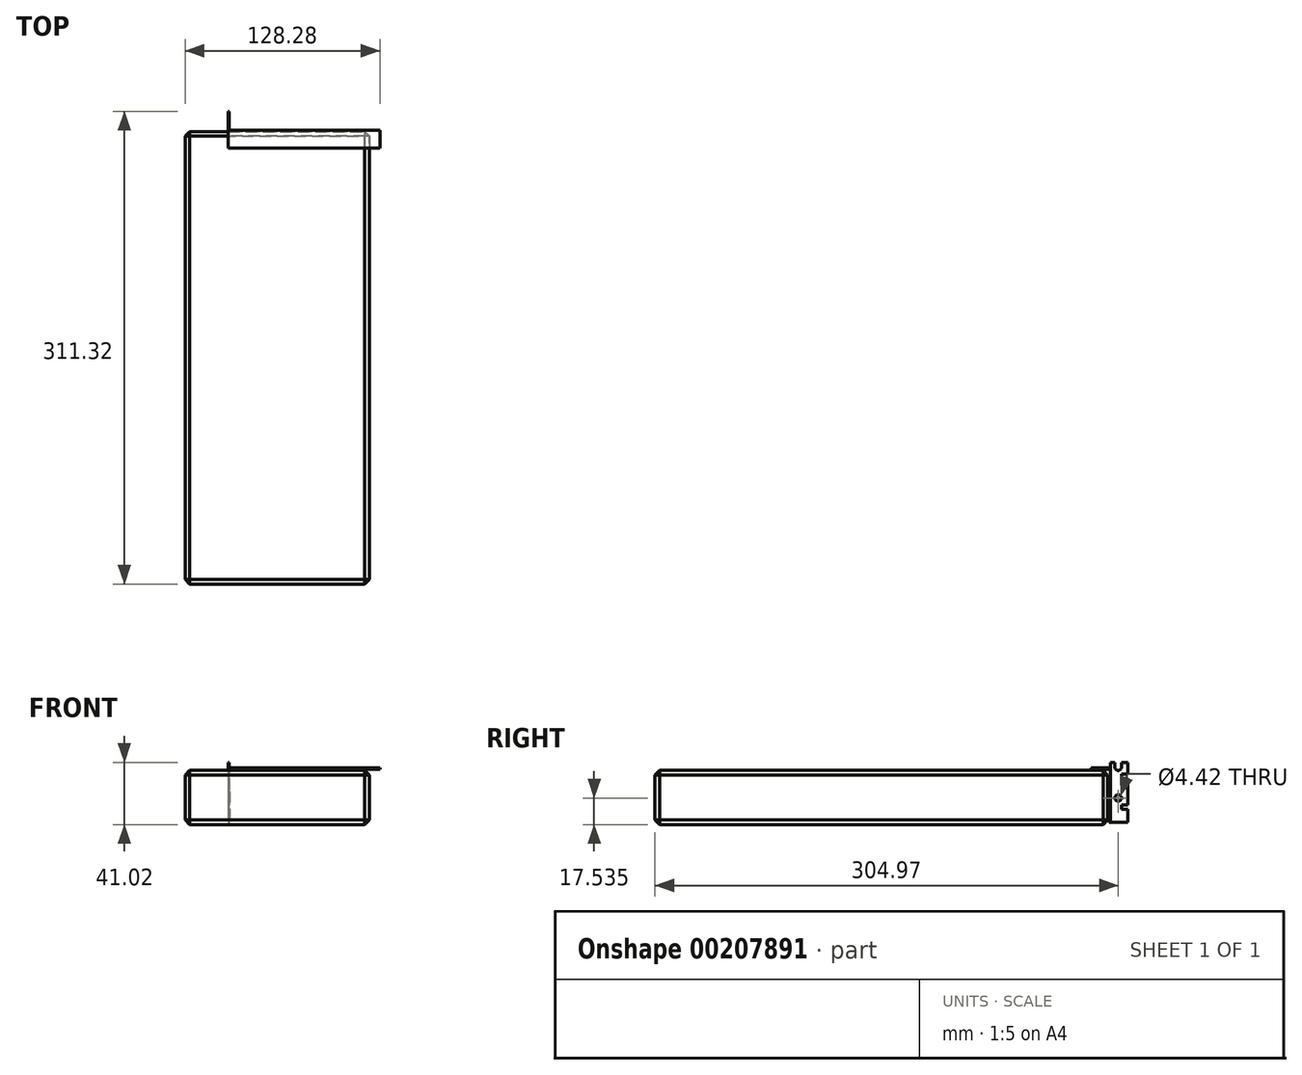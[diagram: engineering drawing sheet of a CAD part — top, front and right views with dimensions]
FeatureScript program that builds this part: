
annotation { "Feature Type Name" : "Feature", "Feature Type Description" : "" }
export const myFeature = defineFeature(function(context is Context, id is Id, definition is map)
    precondition{}
    {
        {
            var Q0;
            Q0=qCreatedBy(makeId("Top.planeOp"),FACE);
            var sketch = newSketch(context, id + "F0", { "sketchPlane" : qUnion([Q0])});
            skLineSegment(sketch, "E0.bottom", {"start": v(-137.4, -240.84) * mm, "end": v(-114.55, -240.84) * mm});
            skLineSegment(sketch, "E0.top", {"start": v(-137.4, 57.16) * mm, "end": v(-114.55, 57.16) * mm});
            skLineSegment(sketch, "E0.left", {"start": v(-137.4, -240.84) * mm, "end": v(-137.4, 57.16) * mm});
            skLineSegment(sketch, "E0.right", {"start": v(-114.55, -240.84) * mm, "end": v(-114.55, 57.16) * mm});
            skPoint(sketch, "E1", {"position": v(-3.4, -240.84) * mm});
            skLineSegment(sketch, "E2", {"start": v(11.76, 58.2) * mm, "end": v(11.76, 59.05) * mm});
            skLineSegment(sketch, "E3", {"start": v(11.76, 59.05) * mm, "end": v(-108.26, 59.05) * mm});
            skLineSegment(sketch, "E4", {"start": v(-108.26, 59.05) * mm, "end": v(-108.26, 70.48) * mm});
            skLineSegment(sketch, "E5", {"start": v(-108.26, 70.48) * mm, "end": v(-109.12, 70.48) * mm});
            skLineSegment(sketch, "E6.bottom", {"start": v(-114.55, -240.84) * mm, "end": v(-16.15, -240.84) * mm});
            skLineSegment(sketch, "E6.top", {"start": v(-114.55, 57.16) * mm, "end": v(-16.15, 57.16) * mm});
            skLineSegment(sketch, "E6.right", {"start": v(-16.15, -240.84) * mm, "end": v(-16.15, 57.16) * mm});
            skLineSegment(sketch, "E7.bottom", {"start": v(-16.15, 57.16) * mm, "end": v(-7.9, 57.16) * mm});
            skLineSegment(sketch, "E7.top", {"start": v(-16.15, 42.16) * mm, "end": v(-7.9, 42.16) * mm});
            skLineSegment(sketch, "E7.left", {"start": v(-16.15, 57.16) * mm, "end": v(-16.15, 42.16) * mm});
            skLineSegment(sketch, "E7.right", {"start": v(-7.9, 57.16) * mm, "end": v(-7.9, 42.16) * mm});
            skPoint(sketch, "E8", {"position": v(-7.9, -240.84) * mm});
            skLineSegment(sketch, "E9.bottom", {"start": v(-16.15, 23.8) * mm, "end": v(-7.9, 23.8) * mm});
            skLineSegment(sketch, "E9.top", {"start": v(-16.15, 15.8) * mm, "end": v(-7.9, 15.8) * mm});
            skLineSegment(sketch, "E9.left", {"start": v(-16.15, 23.8) * mm, "end": v(-16.15, 15.8) * mm});
            skLineSegment(sketch, "E9.right", {"start": v(-7.9, 23.8) * mm, "end": v(-7.9, 15.8) * mm});
            skPoint(sketch, "E10", {"position": v(-3.4, 57.16) * mm});
            skLineSegment(sketch, "E11", {"start": v(-16.15, 12.15) * mm, "end": v(-3.4, 12.15) * mm});
            skLineSegment(sketch, "E12", {"start": v(-3.4, 12.15) * mm, "end": v(-3.4, 0.95) * mm});
            skLineSegment(sketch, "E13", {"start": v(-3.4, 0.95) * mm, "end": v(-11.8, 0.95) * mm});
            skLineSegment(sketch, "E14", {"start": v(-11.8, 0.95) * mm, "end": v(-11.8, -0.95) * mm});
            skLineSegment(sketch, "E15", {"start": v(-11.8, -0.95) * mm, "end": v(-3.4, -0.95) * mm});
            skLineSegment(sketch, "E16", {"start": v(-3.4, -0.95) * mm, "end": v(-3.4, -72.15) * mm});
            skLineSegment(sketch, "E17", {"start": v(-3.4, -72.15) * mm, "end": v(-16.15, -72.15) * mm});
            skPoint(sketch, "E18", {"position": v(-11.8, 0) * mm});
            skArc(sketch, "E19", {"start": v(-14.32, 15.8) * mm, "mid": v(-16.15, 13.98) * mm, "end": v(-14.32, 12.15) * mm});
            skArc(sketch, "E20", {"start": v(-10.85, 0.95) * mm, "mid": v(-11.8, 0) * mm, "end": v(-10.85, -0.95) * mm});
            skLineSegment(sketch, "E21", {"start": v(-16.15, -81.9) * mm, "end": v(-11.35, -81.9) * mm});
            skLineSegment(sketch, "E22", {"start": v(-11.35, -81.9) * mm, "end": v(-11.35, -87.6) * mm});
            skLineSegment(sketch, "E23", {"start": v(-11.35, -87.6) * mm, "end": v(-8.77, -87.6) * mm});
            skLineSegment(sketch, "E24", {"start": v(-8.77, -87.6) * mm, "end": v(-6.35, -86.2) * mm});
            skLineSegment(sketch, "E25", {"start": v(-6.35, -86.2) * mm, "end": v(-6.35, -74.9) * mm});
            skLineSegment(sketch, "E26", {"start": v(-6.35, -74.9) * mm, "end": v(-12.38, -74.9) * mm});
            skLineSegment(sketch, "E27", {"start": v(-12.38, -74.9) * mm, "end": v(-12.38, -72.15) * mm});
            skArc(sketch, "E28", {"start": v(-11, -72.15) * mm, "mid": v(-12.38, -73.53) * mm, "end": v(-11, -74.9) * mm});
            skLineSegment(sketch, "E29", {"start": v(-108.26, 59.05) * mm, "end": v(-109.12, 59.05) * mm});
            skLineSegment(sketch, "E30", {"start": v(-109.12, 70.48) * mm, "end": v(-109.12, 59.05) * mm});
            skLineSegment(sketch, "E31", {"start": v(-109.12, 58.2) * mm, "end": v(-109.12, 59.05) * mm});
            skLineSegment(sketch, "E32", {"start": v(-108.26, 59.05) * mm, "end": v(-108.26, 58.2) * mm});
            skLineSegment(sketch, "E33", {"start": v(-108.26, 58.2) * mm, "end": v(-109.12, 58.2) * mm});
            skLineSegment(sketch, "E34", {"start": v(-108.26, 58.2) * mm, "end": v(11.76, 58.2) * mm});
            skPoint(sketch, "E35", {"position": v(0, 0) * mm});
            skPoint(sketch, "E36", {"position": v(0, 57.16) * mm});
            skSolve(sketch);
        }
        {
            var Q0;
            {var subQ7=sQuery(id+"F0.wireOp",EDGE,"E6.bottom");Q0=makeQuery(id+"F0.imprint","IMPRINT",FACE,{"disambiguationData":[TD([[makeQuery(id+"F0.imprint","IMPRINT",EDGE,{"derivedFrom":subQ7}),1.0]])]});}
            var Q1;
            Q1=makeQuery(id+"F0.imprint","IMPRINT",FACE,{"disambiguationData":[TD([[makeQuery(id+"F0.imprint","IMPRINT",EDGE,{"derivedFrom":sQuery(id+"F0.wireOp",EDGE,"E0.bottom")}),1.0]])]});
            var Q2;
            {var subQ5=sQuery(id+"F0.wireOp",EDGE,"E21");Q2=makeQuery(id+"F0.imprint","IMPRINT",FACE,{"disambiguationData":[TD([[makeQuery(id+"F0.imprint","IMPRINT",EDGE,{"derivedFrom":subQ5}),1.0]])]});}
            var Q3;
            {var subQ0=sQuery(id+"F0.wireOp",EDGE,"E27");var subQ1=sQuery(id+"F0.wireOp",EDGE,"E26");var subQ2=makeQuery(id+"F0.imprint","INTERSECT",VERTEX,{"derivedFrom":[subQ1,subQ0]});Q3=makeQuery(id+"F0.imprint","IMPRINT",FACE,{"disambiguationData":[TD([[makeQuery(id+"F0.imprint","IMPRINT",EDGE,{"disambiguationData":[TD([[subQ2,1.0]])],"derivedFrom":subQ1}),-1.0]])]});}
            var Q4;
            {var subQ0=sQuery(id+"F0.wireOp",EDGE,"E27");var subQ1=sQuery(id+"F0.wireOp",EDGE,"E17");var subQ2=makeQuery(id+"F0.imprint","INTERSECT",VERTEX,{"derivedFrom":[subQ1,subQ0]});Q4=makeQuery(id+"F0.imprint","IMPRINT",FACE,{"disambiguationData":[TD([[makeQuery(id+"F0.imprint","IMPRINT",EDGE,{"disambiguationData":[TD([[subQ2,1.0]])],"derivedFrom":subQ1}),1.0]])]});}
            var Q5;
            {var subQ0=sQuery(id+"F0.wireOp",EDGE,"E15");var subQ1=sQuery(id+"F0.wireOp",EDGE,"E14");var subQ2=makeQuery(id+"F0.imprint","INTERSECT",VERTEX,{"derivedFrom":[subQ1,subQ0]});Q5=makeQuery(id+"F0.imprint","IMPRINT",FACE,{"disambiguationData":[TD([[makeQuery(id+"F0.imprint","IMPRINT",EDGE,{"disambiguationData":[TD([[subQ2,1.0]])],"derivedFrom":subQ1}),1.0]])]});}
            var Q6;
            {var subQ0=sQuery(id+"F0.wireOp",EDGE,"E14");var subQ1=sQuery(id+"F0.wireOp",EDGE,"E13");var subQ2=makeQuery(id+"F0.imprint","INTERSECT",VERTEX,{"derivedFrom":[subQ1,subQ0]});Q6=makeQuery(id+"F0.imprint","IMPRINT",FACE,{"disambiguationData":[TD([[makeQuery(id+"F0.imprint","IMPRINT",EDGE,{"disambiguationData":[TD([[subQ2,1.0]])],"derivedFrom":subQ1}),1.0]])]});}
            var Q7;
            {var subQ7=sQuery(id+"F0.wireOp",EDGE,"E12");Q7=makeQuery(id+"F0.imprint","IMPRINT",FACE,{"disambiguationData":[TD([[makeQuery(id+"F0.imprint","IMPRINT",EDGE,{"derivedFrom":subQ7}),-1.0]])]});}
            var Q8;
            {var subQ0=sQuery(id+"F0.wireOp",EDGE,"E11");var subQ1=sQuery(id+"F0.wireOp",EDGE,"E6.right");var subQ2=makeQuery(id+"F0.imprint","INTERSECT",VERTEX,{"derivedFrom":[subQ1,subQ0]});Q8=makeQuery(id+"F0.imprint","IMPRINT",FACE,{"disambiguationData":[TD([[makeQuery(id+"F0.imprint","IMPRINT",EDGE,{"disambiguationData":[TD([[subQ2,-1.0]])],"derivedFrom":subQ1}),-1.0]])]});}
            var Q9;
            {var subQ0=sQuery(id+"F0.wireOp",EDGE,"E9.top");var subQ3=sQuery(id+"F0.wireOp",EDGE,"E19");var subQ5=makeQuery(id+"F0.imprint","INTERSECT",VERTEX,{"derivedFrom":[subQ0,subQ3]});Q9=makeQuery(id+"F0.imprint","IMPRINT",FACE,{"disambiguationData":[TD([[makeQuery(id+"F0.imprint","IMPRINT",EDGE,{"disambiguationData":[TD([[subQ5,-1.0]])],"derivedFrom":subQ3}),-1.0]])]});}
            var Q10;
            Q10=makeQuery(id+"F0.imprint","IMPRINT",FACE,{"disambiguationData":[TD([[makeQuery(id+"F0.imprint","IMPRINT",EDGE,{"derivedFrom":sQuery(id+"F0.wireOp",EDGE,"E9.bottom")}),-1.0]])]});
            var Q11;
            Q11=makeQuery(id+"F0.imprint","IMPRINT",FACE,{"disambiguationData":[TD([[makeQuery(id+"F0.imprint","IMPRINT",EDGE,{"derivedFrom":sQuery(id+"F0.wireOp",EDGE,"E7.bottom")}),-1.0]])]});
            extrude(context, id + "F1", {"entities" : qUnion([Q0, Q1, Q2, Q3, Q4, Q5, Q6, Q7, Q8, Q9, Q10, Q11]), "endBound" : BoundingType.SYMMETRIC, "depth" : 1.57 * mm});
        }
        {
            var Q0;
            Q0=makeQuery(id+"F0.imprint","IMPRINT",FACE,{"disambiguationData":[TD([[makeQuery(id+"F0.imprint","IMPRINT",EDGE,{"derivedFrom":sQuery(id+"F0.wireOp",EDGE,"E2")}),1.0]])]});
            extrude(context, id + "F2", {"entities" : qUnion([Q0]), "depth" : 10 * mm, "hasSecondDirection" : true, "secondDirectionOppositeDirection" : true, "secondDirectionDepth" : 40 * mm});
        }
        {
            var Q0;
            Q0=makeQuery(id+"F2.opExtrude","SWEPT_FACE",FACE,{"disambiguationData":[OSD([sQuery(id+"F0.wireOp",EDGE,"E3")])]});
            var sketch = newSketch(context, id + "F3", { "sketchPlane" : qUnion([Q0])});
            skLineSegment(sketch, "E37", {"start": v(-4.49, -2.06) * mm, "end": v(-11.76, -2.06) * mm});
            skLineSegment(sketch, "E38", {"start": v(-11.76, -2.06) * mm, "end": v(-11.76, -12.25) * mm});
            skLineSegment(sketch, "E39", {"start": v(-11.76, -12.25) * mm, "end": v(-4.49, -12.25) * mm});
            skLineSegment(sketch, "E40", {"start": v(-4.49, -12.25) * mm, "end": v(-0.38, -16.37) * mm});
            skLineSegment(sketch, "E41", {"start": v(-0.38, -16.36) * mm, "end": v(101.78, -16.36) * mm});
            skLineSegment(sketch, "E42", {"start": v(108.26, -13.82) * mm, "end": v(108.26, 5.23) * mm});
            skLineSegment(sketch, "E43", {"start": v(108.26, 5.23) * mm, "end": v(105.34, 5.23) * mm});
            skLineSegment(sketch, "E44", {"start": v(103.7, 2.06) * mm, "end": v(-0.37, 2.05) * mm});
            skLineSegment(sketch, "E45", {"start": v(-0.37, 2.05) * mm, "end": v(-4.49, -2.06) * mm});
            skLineSegment(sketch, "E46.bottom", {"start": v(7.9, 0.79) * mm, "end": v(114.55, 0.79) * mm});
            skLineSegment(sketch, "E46.top", {"start": v(7.9, -0.78) * mm, "end": v(114.55, -0.78) * mm});
            skLineSegment(sketch, "E46.left", {"start": v(7.9, 0.78) * mm, "end": v(7.9, -0.78) * mm});
            skLineSegment(sketch, "E46.right", {"start": v(114.55, 0.79) * mm, "end": v(114.55, -0.78) * mm});
            skPoint(sketch, "E47", {"position": v(7.9, 0) * mm});
            skLineSegment(sketch, "E48", {"start": v(108.26, -13.82) * mm, "end": v(104.32, -13.82) * mm});
            skLineSegment(sketch, "E49", {"start": v(104.32, -13.82) * mm, "end": v(101.78, -16.36) * mm});
            skLineSegment(sketch, "E50", {"start": v(103.7, 2.05) * mm, "end": v(103.7, 3.59) * mm});
            skLineSegment(sketch, "E51", {"start": v(103.7, 3.59) * mm, "end": v(105.34, 5.23) * mm});
            skPoint(sketch, "E52", {"position": v(0, 0) * mm});
            skLineSegment(sketch, "E53", {"start": v(-11.76, -22.39) * mm, "end": v(-11.76, -32.58) * mm});
            skLineSegment(sketch, "E54", {"start": v(-11.76, -32.57) * mm, "end": v(-4.49, -32.57) * mm});
            skLineSegment(sketch, "E55", {"start": v(-4.49, -32.57) * mm, "end": v(-0.38, -36.69) * mm});
            skLineSegment(sketch, "E56", {"start": v(-0.38, -36.69) * mm, "end": v(101.78, -36.68) * mm});
            skLineSegment(sketch, "E57", {"start": v(104.32, -34.14) * mm, "end": v(101.78, -36.68) * mm});
            skLineSegment(sketch, "E58", {"start": v(104.32, -34.14) * mm, "end": v(108.26, -34.14) * mm});
            skLineSegment(sketch, "E59", {"start": v(108.26, -34.14) * mm, "end": v(108.26, -15.1) * mm});
            skLineSegment(sketch, "E60", {"start": v(108.26, -15.1) * mm, "end": v(105.34, -15.1) * mm});
            skLineSegment(sketch, "E61", {"start": v(105.34, -15.1) * mm, "end": v(103.7, -16.73) * mm});
            skLineSegment(sketch, "E62", {"start": v(103.7, -16.73) * mm, "end": v(103.7, -18.26) * mm});
            skLineSegment(sketch, "E63", {"start": v(103.7, -18.26) * mm, "end": v(-0.37, -18.27) * mm});
            skLineSegment(sketch, "E64", {"start": v(-11.76, -22.39) * mm, "end": v(-4.49, -22.39) * mm});
            skLineSegment(sketch, "E65", {"start": v(-4.49, -22.39) * mm, "end": v(-0.37, -18.27) * mm});
            skLineSegment(sketch, "E66", {"start": v(-0.38, -16.37) * mm, "end": v(-0.37, -18.27) * mm});
            skLineSegment(sketch, "E67", {"start": v(108.26, -13.82) * mm, "end": v(108.26, -15.1) * mm});
            skSolve(sketch);
        }
        {
            var Q0;
            Q0 = qSketchRegion(id + "F3", true);
            extrude(context, id + "F4", {"entities" : qUnion([Q0]), "operationType" : NewBodyOperationType.INTERSECT, "oppositeDirection" : true, "depth" : 5 * mm});
        }
        {
            var Q0;
            Q0=makeQuery(id+"F0.imprint","IMPRINT",FACE,{"disambiguationData":[TD([[makeQuery(id+"F0.imprint","IMPRINT",EDGE,{"derivedFrom":sQuery(id+"F0.wireOp",EDGE,"E29")}),1.0]])]});
            var Q1;
            Q1=makeQuery(id+"F0.imprint","IMPRINT",FACE,{"disambiguationData":[TD([[makeQuery(id+"F0.imprint","IMPRINT",EDGE,{"derivedFrom":sQuery(id+"F0.wireOp",EDGE,"E4")}),1.0]])]});
            extrude(context, id + "F5", {"entities" : qUnion([Q0, Q1]), "depth" : 10 * mm, "hasSecondDirection" : true, "secondDirectionOppositeDirection" : true, "secondDirectionDepth" : 40 * mm});
        }
        {
            var Q0;
            Q0=makeQuery(id+"F5.opExtrude","SWEPT_FACE",FACE,{"disambiguationData":[OSD([sQuery(id+"F0.wireOp",EDGE,"E30"),sQuery(id+"F0.wireOp",EDGE,"E31")])]});
            var sketch = newSketch(context, id + "F6", { "sketchPlane" : qUnion([Q0])});
            skLineSegment(sketch, "E68", {"start": v(-70.48, 5.23) * mm, "end": v(-70.48, -2.4) * mm});
            skLineSegment(sketch, "E69", {"start": v(-70.48, -2.4) * mm, "end": v(-66.29, -2.4) * mm});
            skLineSegment(sketch, "E70", {"start": v(-66.3, -2.4) * mm, "end": v(-66.3, -5.44) * mm});
            skLineSegment(sketch, "E71", {"start": v(-66.3, -5.44) * mm, "end": v(-70.48, -5.44) * mm});
            skLineSegment(sketch, "E72", {"start": v(-70.48, -5.44) * mm, "end": v(-70.48, -13.83) * mm});
            skLineSegment(sketch, "E73", {"start": v(-58.19, -13.83) * mm, "end": v(-58.19, 5.22) * mm});
            skLineSegment(sketch, "E74", {"start": v(-61.92, 5.22) * mm, "end": v(-61.92, -0.16) * mm});
            skLineSegment(sketch, "E75", {"start": v(-61.92, -0.15) * mm, "end": v(-66.34, -0.16) * mm});
            skLineSegment(sketch, "E76", {"start": v(-66.34, -0.16) * mm, "end": v(-66.34, 5.23) * mm});
            skLineSegment(sketch, "E77", {"start": v(-66.34, 5.23) * mm, "end": v(-70.48, 5.23) * mm});
            skPoint(sketch, "E78", {"position": v(-70.48, -16.37) * mm});
            skArc(sketch, "E79", {"start": v(-66.34, 2.06) * mm, "mid": v(-64.13, -0.16) * mm, "end": v(-61.92, 2.06) * mm});
            skLineSegment(sketch, "E80.bottom", {"start": v(-57.16, 0.79) * mm, "end": v(0, 0.79) * mm});
            skLineSegment(sketch, "E80.top", {"start": v(-57.16, -0.79) * mm, "end": v(0, -0.79) * mm});
            skLineSegment(sketch, "E80.left", {"start": v(-57.16, 0.79) * mm, "end": v(-57.16, -0.79) * mm});
            skPoint(sketch, "E81", {"position": v(-57.16, 0) * mm});
            skLineSegment(sketch, "E82.bottom", {"start": v(-46.48, 1.65) * mm, "end": v(-58.19, 1.65) * mm});
            skLineSegment(sketch, "E82.top", {"start": v(-46.48, 0.78) * mm, "end": v(-58.19, 0.78) * mm});
            skLineSegment(sketch, "E82.left", {"start": v(-46.48, 1.65) * mm, "end": v(-46.48, 0.78) * mm});
            skLineSegment(sketch, "E82.right", {"start": v(-58.19, 1.65) * mm, "end": v(-58.19, 0.78) * mm});
            skLineSegment(sketch, "E83", {"start": v(-59.05, 5.22) * mm, "end": v(-59.05, -13.83) * mm});
            skLineSegment(sketch, "E84", {"start": v(-61.92, 5.22) * mm, "end": v(-59.05, 5.22) * mm});
            skLineSegment(sketch, "E85", {"start": v(-59.05, 5.22) * mm, "end": v(-58.19, 5.22) * mm});
            skPoint(sketch, "E86", {"position": v(0, 0) * mm});
            skLineSegment(sketch, "E87", {"start": v(-59.05, -15.1) * mm, "end": v(-70.48, -15.1) * mm});
            skLineSegment(sketch, "E88", {"start": v(-70.48, -15.1) * mm, "end": v(-70.48, -22.71) * mm});
            skLineSegment(sketch, "E89", {"start": v(-70.48, -22.71) * mm, "end": v(-66.3, -22.71) * mm});
            skLineSegment(sketch, "E90", {"start": v(-66.3, -22.71) * mm, "end": v(-66.3, -25.76) * mm});
            skLineSegment(sketch, "E91", {"start": v(-66.3, -25.76) * mm, "end": v(-70.48, -25.76) * mm});
            skLineSegment(sketch, "E92", {"start": v(-70.48, -25.76) * mm, "end": v(-70.48, -34.14) * mm});
            skLineSegment(sketch, "E93", {"start": v(-70.48, -34.14) * mm, "end": v(-59.05, -34.14) * mm});
            skLineSegment(sketch, "E94", {"start": v(-59.05, -34.14) * mm, "end": v(-59.05, -15.1) * mm});
            skLineSegment(sketch, "E95.bottom", {"start": v(-59.05, -15.1) * mm, "end": v(-58.19, -15.1) * mm});
            skLineSegment(sketch, "E95.top", {"start": v(-59.05, -34.14) * mm, "end": v(-58.19, -34.14) * mm});
            skLineSegment(sketch, "E95.left", {"start": v(-59.05, -15.1) * mm, "end": v(-59.05, -34.14) * mm});
            skLineSegment(sketch, "E95.right", {"start": v(-58.19, -15.1) * mm, "end": v(-58.19, -34.14) * mm});
            skLineSegment(sketch, "E96", {"start": v(-59.05, -13.83) * mm, "end": v(-70.48, -13.83) * mm});
            skLineSegment(sketch, "E97", {"start": v(-59.05, -13.83) * mm, "end": v(-58.19, -13.83) * mm});
            skLineSegment(sketch, "E98.bottom", {"start": v(-70.48, -13.83) * mm, "end": v(-58.19, -13.83) * mm});
            skLineSegment(sketch, "E98.top", {"start": v(-70.48, -15.1) * mm, "end": v(-58.19, -15.1) * mm});
            skLineSegment(sketch, "E98.left", {"start": v(-70.48, -13.83) * mm, "end": v(-70.48, -15.1) * mm});
            skLineSegment(sketch, "E98.right", {"start": v(-58.19, -13.83) * mm, "end": v(-58.19, -15.1) * mm});
            skCircle(sketch, "E99", {"center": v(-64.13, -18.27) * mm, "radius": 2.2 * mm});
            skSolve(sketch);
        }
        {
            var Q0;
            {var subQ0=sQuery(id+"F6.wireOp",EDGE,"E76");var subQ1=sQuery(id+"F6.wireOp",EDGE,"E75");var subQ2=makeQuery(id+"F6.imprint","INTERSECT",VERTEX,{"derivedFrom":[subQ1,subQ0]});Q0=makeQuery(id+"F6.imprint","IMPRINT",FACE,{"disambiguationData":[TD([[makeQuery(id+"F6.imprint","IMPRINT",EDGE,{"disambiguationData":[TD([[subQ2,1.0]])],"derivedFrom":subQ1}),-1.0]])]});}
            var Q1;
            Q1=makeQuery(id+"F6.imprint","IMPRINT",FACE,{"disambiguationData":[TD([[makeQuery(id+"F6.imprint","IMPRINT",EDGE,{"derivedFrom":sQuery(id+"F6.wireOp",EDGE,"E68")}),1.0]])]});
            var Q2;
            {var subQ0=sQuery(id+"F6.wireOp",EDGE,"E75");var subQ1=sQuery(id+"F6.wireOp",EDGE,"E74");var subQ2=makeQuery(id+"F6.imprint","INTERSECT",VERTEX,{"derivedFrom":[subQ1,subQ0]});Q2=makeQuery(id+"F6.imprint","IMPRINT",FACE,{"disambiguationData":[TD([[makeQuery(id+"F6.imprint","IMPRINT",EDGE,{"disambiguationData":[TD([[subQ2,1.0]])],"derivedFrom":subQ1}),-1.0]])]});}
            var Q3;
            {var subQ3=sQuery(id+"F6.wireOp",EDGE,"E82.right");Q3=makeQuery(id+"F6.imprint","IMPRINT",FACE,{"disambiguationData":[TD([[makeQuery(id+"F6.imprint","IMPRINT",EDGE,{"derivedFrom":subQ3}),-1.0]])]});}
            var Q4;
            {var subQ0=sQuery(id+"F6.wireOp",EDGE,"E98.left");Q4=makeQuery(id+"F6.imprint","IMPRINT",FACE,{"disambiguationData":[TD([[makeQuery(id+"F6.imprint","IMPRINT",EDGE,{"derivedFrom":subQ0}),1.0]])]});}
            var Q5;
            {var subQ0=sQuery(id+"F6.wireOp",EDGE,"E88");Q5=makeQuery(id+"F6.imprint","IMPRINT",FACE,{"disambiguationData":[TD([[makeQuery(id+"F6.imprint","IMPRINT",EDGE,{"derivedFrom":subQ0}),1.0]])]});}
            var Q6;
            Q6=makeQuery(id+"F6.imprint","IMPRINT",FACE,{"disambiguationData":[TD([[makeQuery(id+"F6.imprint","IMPRINT",EDGE,{"derivedFrom":sQuery(id+"F6.wireOp",EDGE,"E95.top")}),1.0]])]});
            extrude(context, id + "F7", {"entities" : qUnion([Q0, Q1, Q2, Q3, Q4, Q5, Q6]), "operationType" : NewBodyOperationType.INTERSECT, "oppositeDirection" : true, "depth" : 1 * mm});
        }
        {
            var Q0;
            Q0=makeQuery(id+"F6.imprint","IMPRINT",FACE,{"disambiguationData":[TD([[makeQuery(id+"F6.imprint","IMPRINT",EDGE,{"derivedFrom":sQuery(id+"F6.wireOp",EDGE,"E82.bottom")}),1.0]])]});
            extrude(context, id + "F8", {"entities" : qUnion([Q0]), "oppositeDirection" : true, "depth" : 100 * mm});
        }
        {
            var Q0;
            {var subQ7=sQuery(id+"F0.wireOp",EDGE,"E6.bottom");Q0=makeQuery(id+"F0.imprint","IMPRINT",FACE,{"disambiguationData":[TD([[makeQuery(id+"F0.imprint","IMPRINT",EDGE,{"derivedFrom":subQ7}),1.0]])]});}
            var Q1;
            Q1=makeQuery(id+"F0.imprint","IMPRINT",FACE,{"disambiguationData":[TD([[makeQuery(id+"F0.imprint","IMPRINT",EDGE,{"derivedFrom":sQuery(id+"F0.wireOp",EDGE,"E0.bottom")}),1.0]])]});
            extrude(context, id + "F9", {"entities" : qUnion([Q0, Q1]), "oppositeDirection" : true, "depth" : 35.8 * mm});
        }
        {
            var Q0;
            Q0=makeQuery(id+"F9.opExtrude","CAP_EDGE",EDGE,{"disambiguationData":[OSD([sQuery(id+"F0.wireOp",EDGE,"E6.right"),sQuery(id+"F0.wireOp",EDGE,"E7.left"),sQuery(id+"F0.wireOp",EDGE,"E9.left")])],"isStart":false});
            var Q1;
            Q1=makeQuery(id+"F9.opExtrude","CAP_EDGE",EDGE,{"disambiguationData":[OSD([sQuery(id+"F0.wireOp",EDGE,"E0.left")])],"isStart":false});
            var Q2;
            Q2=makeQuery(id+"F9.opExtrude","CAP_EDGE",EDGE,{"disambiguationData":[OSD([sQuery(id+"F0.wireOp",EDGE,"E0.left")])],"isStart":true});
            var Q3;
            Q3=makeQuery(id+"F9.opExtrude","CAP_EDGE",EDGE,{"disambiguationData":[OSD([sQuery(id+"F0.wireOp",EDGE,"E6.right"),sQuery(id+"F0.wireOp",EDGE,"E7.left"),sQuery(id+"F0.wireOp",EDGE,"E9.left")])],"isStart":true});
            var Q4;
            Q4=makeQuery(id+"F9.opExtrude","CAP_EDGE",EDGE,{"disambiguationData":[OSD([sQuery(id+"F0.wireOp",EDGE,"E0.bottom"),sQuery(id+"F0.wireOp",EDGE,"E6.bottom")])],"isStart":true});
            var Q5;
            Q5=makeQuery(id+"F9.opExtrude","CAP_EDGE",EDGE,{"disambiguationData":[OSD([sQuery(id+"F0.wireOp",EDGE,"E0.bottom"),sQuery(id+"F0.wireOp",EDGE,"E6.bottom")])],"isStart":false});
            var Q6;
            Q6=makeQuery(id+"F9.opExtrude","CAP_EDGE",EDGE,{"disambiguationData":[OSD([sQuery(id+"F0.wireOp",EDGE,"E0.top"),sQuery(id+"F0.wireOp",EDGE,"E6.top")])],"isStart":false});
            var Q7;
            Q7=makeQuery(id+"F9.opExtrude","CAP_EDGE",EDGE,{"disambiguationData":[OSD([sQuery(id+"F0.wireOp",EDGE,"E0.top"),sQuery(id+"F0.wireOp",EDGE,"E6.top")])],"isStart":true});
            var Q8;
            Q8=makeQuery(id+"F9.opExtrude","SWEPT_EDGE",EDGE,{"disambiguationData":[OSD([sQuery(id+"F0.wireOp",EDGE,"E0.top"),sQuery(id+"F0.wireOp",EDGE,"E0.left")])]});
            var Q9;
            Q9=makeQuery(id+"F9.opExtrude","SWEPT_EDGE",EDGE,{"disambiguationData":[OSD([sQuery(id+"F0.wireOp",EDGE,"E6.top"),sQuery(id+"F0.wireOp",EDGE,"E7.bottom"),sQuery(id+"F0.wireOp",EDGE,"E7.left")])]});
            var Q10;
            Q10=makeQuery(id+"F9.opExtrude","SWEPT_EDGE",EDGE,{"disambiguationData":[OSD([sQuery(id+"F0.wireOp",EDGE,"E6.bottom"),sQuery(id+"F0.wireOp",EDGE,"E6.right")])]});
            var Q11;
            Q11=makeQuery(id+"F9.opExtrude","SWEPT_EDGE",EDGE,{"disambiguationData":[OSD([sQuery(id+"F0.wireOp",EDGE,"E0.bottom"),sQuery(id+"F0.wireOp",EDGE,"E0.left")])]});
            chamfer(context, id + "F10", {"entities" : qUnion([Q0, Q1, Q2, Q3, Q4, Q5, Q6, Q7, Q8, Q9, Q10, Q11]), "width" : 3 * mm, "tangentPropagation" : true});
        }
    });
